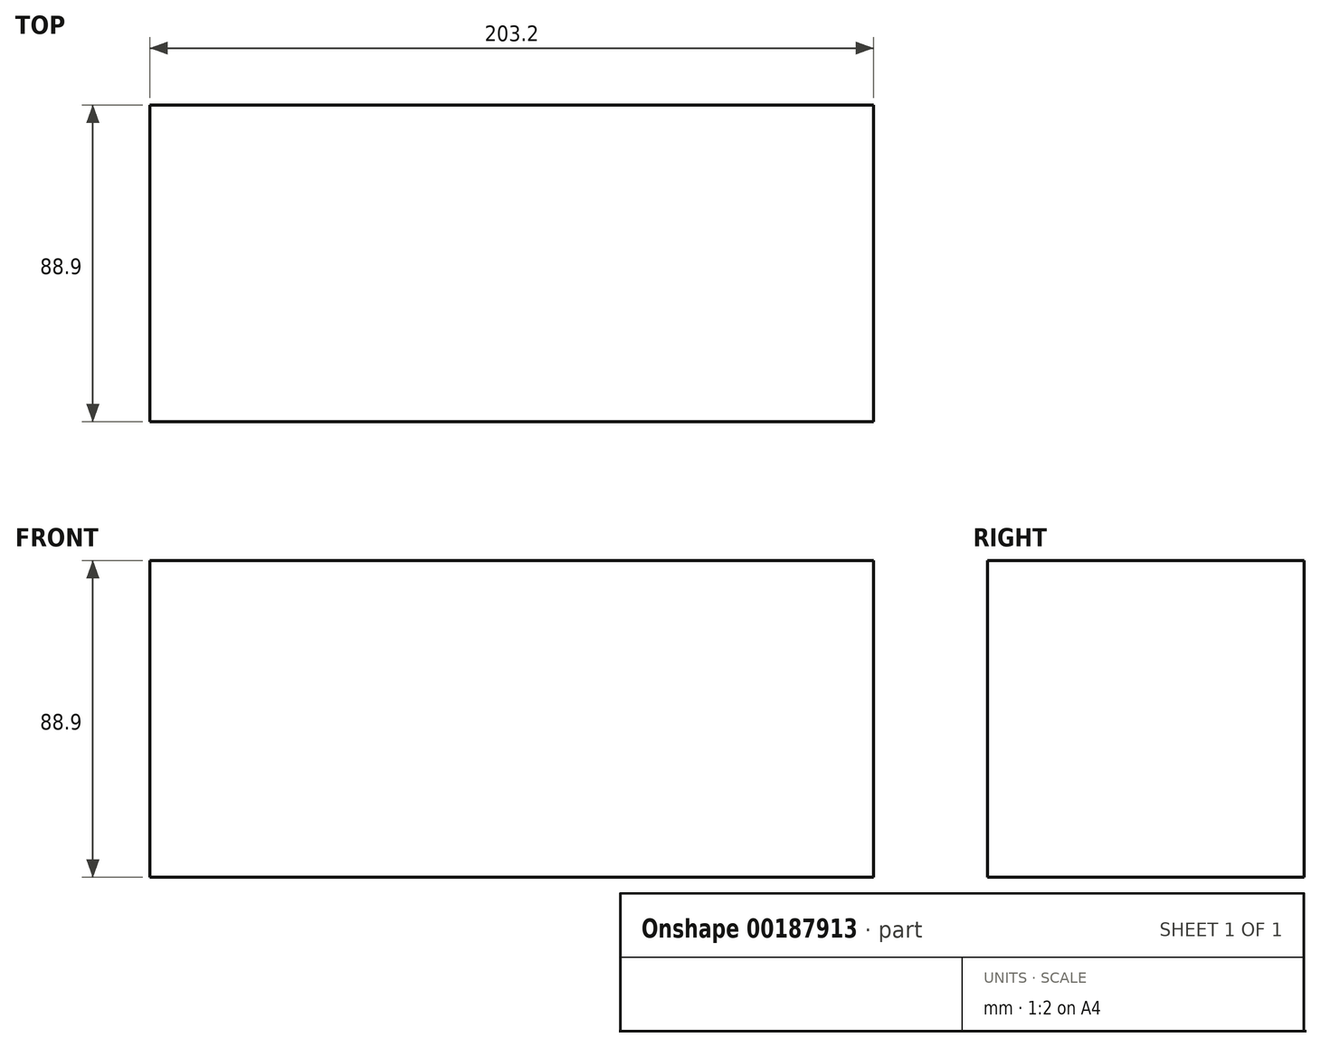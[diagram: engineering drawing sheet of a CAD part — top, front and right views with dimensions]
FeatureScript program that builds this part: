
annotation { "Feature Type Name" : "Feature", "Feature Type Description" : "" }
export const myFeature = defineFeature(function(context is Context, id is Id, definition is map)
    precondition{}
    {
        {
            var Q0;
            Q0=qCreatedBy(makeId("Right.planeOp"),FACE);
            var sketch = newSketch(context, id + "F0", { "sketchPlane" : qUnion([Q0])});
            skLineSegment(sketch, "E0.bottom", {"start": v(44.45, 44.45) * mm, "end": v(-44.45, 44.45) * mm});
            skLineSegment(sketch, "E0.top", {"start": v(44.45, -44.45) * mm, "end": v(-44.45, -44.45) * mm});
            skLineSegment(sketch, "E0.left", {"start": v(44.45, 44.45) * mm, "end": v(44.45, -44.45) * mm});
            skLineSegment(sketch, "E0.right", {"start": v(-44.45, 44.45) * mm, "end": v(-44.45, -44.45) * mm});
            skPoint(sketch, "E0.middle", {"position": v(0, 0) * mm});
            skSolve(sketch);
        }
        {
            var Q0;
            Q0=makeQuery(id+"F0.imprint","IMPRINT",FACE,{"disambiguationData":[TD([[makeQuery(id+"F0.imprint","IMPRINT",EDGE,{"derivedFrom":sQuery(id+"F0.wireOp",EDGE,"E0.bottom")}),1.0]])]});
            extrude(context, id + "F1", {"entities" : qUnion([Q0]), "depth" : 203.2 * mm});
        }
    });
